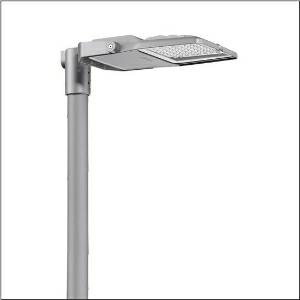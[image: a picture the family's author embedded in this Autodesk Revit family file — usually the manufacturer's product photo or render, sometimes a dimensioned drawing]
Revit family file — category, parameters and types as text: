
# Revit family: floodlight_fl_21_iq_mini___pl33t_5xa7771d2f3a_c3c2
name_source: partatom
category: Lighting Fixtures
units: mm (PartAtom-declared; Revit-internal decimal feet)

## family parameters
Cut with Voids When Loaded = No
Host = Face
Light Source = No
Part Type = Normal
Room Calculation Point = No
Round Connector Dimension = Use Diameter
Shared = No

## types (1)
- --- (1 x LED, 17620 lm, 143 W, 3000K)
    Apparent Load = 143 VA
    CIE Flux Codes = 26 75 99 100 100
    Color Rendering = 70
    Color Temperature = 3000K
    Default Elevation = 1800 mm
    Description = Floodlight FL 21 iQ mini, floodlight, primary light control with lens, of PMMA, primary optical cover: protective disc, of toughened safety glass, transparent, light distribution: PL33T, light emission: direct distribution, installation type: surface-mounted, LED, High Power LED, rated luminous flux: 17.620lm, luminous efficacy: 123lm/W, light colour: 730, colour temperature: 3000K, control gear: iQ Comfort/DALI, control: Auto-Match, Temp-Guard, Lumen-Switch, Night-Set, Smart-Wire, Light-Fading, Desk-Remote (wireless, voltage-free reading and setting of iQ features in the workshop via application-optimized NFC function/RFID function), optimised constant luminous flux control (CLO 2.0), with terminal, 6-pole, mains connection: 220..240V, AC, 50/60Hz, start of lifetime: 143W, end of service life: 152W, reduction: 61W, luminaire housing, of diecast aluminium, powder-coated, Siteco® metallic grey (DB 702S), corrosivity category C5 mid according to DIN EN ISO 12944, suitable for swimming pools, chlorine-resistant, sealing non-destructively replaceable, please order mast flange separately, mast bracket, of steel, galvanised, powder-coated, Siteco® metallic grey (DB 702S), protection rating (complete): IP66, insulation class (complete): insulation class II (safety insulation), certification: CE, ENEC, VDE, protection symbol: D, impact resistance: IK08, permissible operating ambient temperature: -40..+40°C, permissible operating ambient temperature for outdoor applications: -40..+50°C, standard: DIN EN 12944, LABS conformity tested according to VDMA 24364:2018-05, packaging unit: 1 piece

Light Distribution: PL33T
    Height = 70 mm
    Lamp = 1 x LED
    Lamp Light Flux = 17620 lm
    Lamp Power = 143 W
    Lamp count = 1
    Length = 485 mm
    Luminous efficacy = 123 lm/W
    Manufacturer = Siteco
    ModVariant = No
    Model = 5XA7771D2F3A
    Number of Poles = 1
    OnlyDefault = Yes
    Power Factor = 1
    Product Name = Floodlight FL 21 iQ mini | PL33T
    Product group = floodlight | pylon annexe
    ProductGroupID = 6201
    Protection Class = Protection class II
    Protection Degree = IP 66
    RLX_Detail_Level = 1
    RLX_Emergency_Light_Flux = 0 lm
    RLX_Emergency_Type = 0
    RLX_Emergency_Type_DB = No
    RlxData = <blob elided: 101517 chars, md5=93e999eb>
    Socket = socket
    Standby Power = 0 W
    System Light Flux = 17620 lm
    System Power = 143 W
    Type Comments = factory setting: luminous flux: 100 % | dim-lin: 254 | 730 mA
    Type Image = l_1007125.jpg
    URL = http://relux.com
    VarID = @adj_170639
    Voltage = 0 V
    Weight = 0.00 kg
    Width = 337 mm

## geometry (parser evidence)
native form markers: Blend x4, Sweep x13
no freeform markers — native parametric forms only
